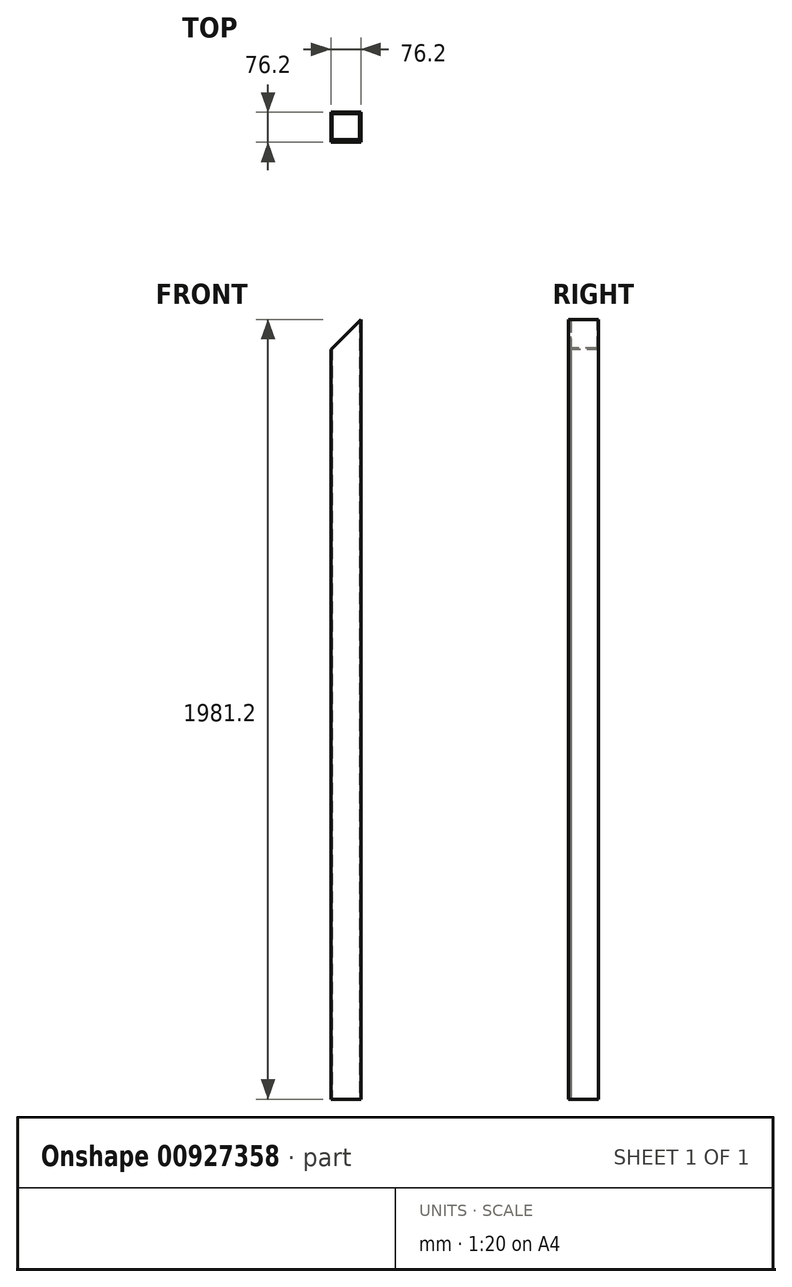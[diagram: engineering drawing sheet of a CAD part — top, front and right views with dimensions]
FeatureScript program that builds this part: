
annotation { "Feature Type Name" : "Feature", "Feature Type Description" : "" }
export const myFeature = defineFeature(function(context is Context, id is Id, definition is map)
    precondition{}
    {
        {
            var Q0;
            Q0=qCreatedBy(makeId("Top.planeOp"),FACE);
            var sketch = newSketch(context, id + "F0", { "sketchPlane" : qUnion([Q0])});
            skLineSegment(sketch, "E0.bottom", {"start": v(-38.1, 38.1) * mm, "end": v(38.1, 38.1) * mm});
            skLineSegment(sketch, "E0.top", {"start": v(-38.1, -38.1) * mm, "end": v(38.1, -38.1) * mm});
            skLineSegment(sketch, "E0.left", {"start": v(-38.1, 38.1) * mm, "end": v(-38.1, -38.1) * mm});
            skLineSegment(sketch, "E0.right", {"start": v(38.1, 38.1) * mm, "end": v(38.1, -38.1) * mm});
            skLineSegment(sketch, "E1.bottom", {"start": v(-34.93, 34.92) * mm, "end": v(34.92, 34.93) * mm});
            skLineSegment(sketch, "E1.top", {"start": v(-34.92, -31.48) * mm, "end": v(34.93, -31.48) * mm});
            skLineSegment(sketch, "E1.left", {"start": v(-34.93, 34.92) * mm, "end": v(-34.92, -31.48) * mm});
            skLineSegment(sketch, "E1.right", {"start": v(34.92, 34.93) * mm, "end": v(34.93, -31.48) * mm});
            skSolve(sketch);
        }
        {
            var Q0;
            Q0=makeQuery(id+"F0.imprint","IMPRINT",FACE,{"disambiguationData":[TD([[makeQuery(id+"F0.imprint","IMPRINT",EDGE,{"derivedFrom":sQuery(id+"F0.wireOp",EDGE,"E0.bottom")}),-1.0]])]});
            extrude(context, id + "F1", {"entities" : qUnion([Q0]), "depth" : 1981.2 * mm, "offsetDistance" : 25.4 * mm});
        }
        {
            var Q0;
            Q0=makeQuery(id+"F1.opExtrude","SWEPT_FACE",FACE,{"disambiguationData":[OSD([sQuery(id+"F0.wireOp",EDGE,"E0.top")])]});
            var sketch = newSketch(context, id + "F2", { "sketchPlane" : qUnion([Q0])});
            skLineSegment(sketch, "E2.MirrorCS", {"start": v(38.1, 1981.2) * mm, "end": v(-138.6, 1804.5) * mm});
            skSolve(sketch);
        }
        {
            var Q0;
            {var subQ1=sQuery(id+"F0.wireOp",EDGE,"E0.top");var subQ2=makeQuery(id+"F1.opExtrude","CAP_EDGE",EDGE,{"disambiguationData":[OSD([subQ1])],"isStart":false});Q0=makeQuery(id+"F2.imprint","IMPRINT",FACE,{"disambiguationData":[TD([[makeQuery(id+"F2.imprint","IMPRINT",EDGE,{"derivedFrom":subQ2}),-1.0]])]});}
            extrude(context, id + "F3", {"entities" : qUnion([Q0]), "operationType" : NewBodyOperationType.REMOVE, "oppositeDirection" : true, "depth" : 101.6 * mm, "offsetDistance" : 25.4 * mm});
        }
    });
